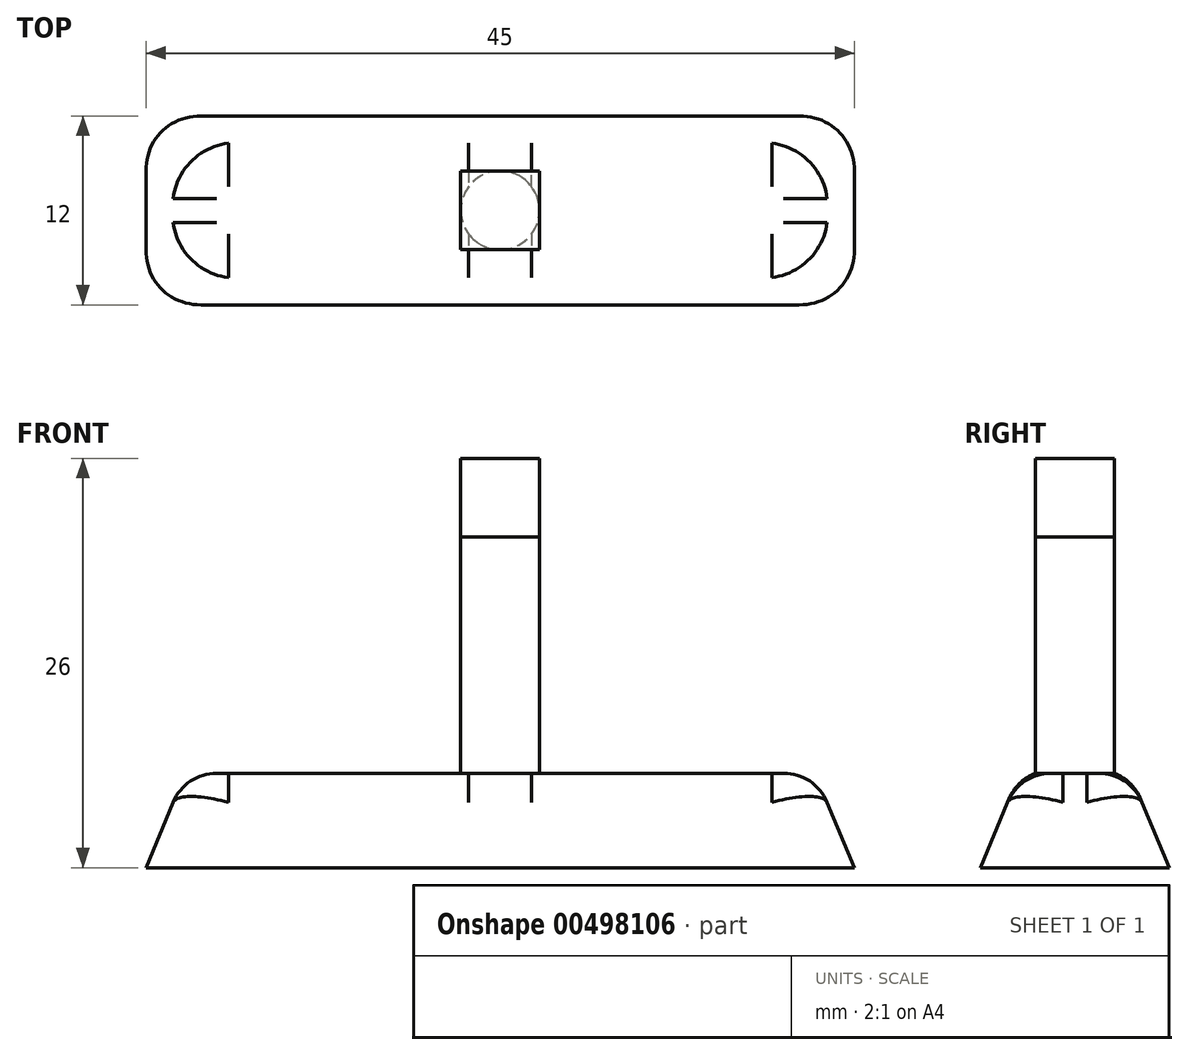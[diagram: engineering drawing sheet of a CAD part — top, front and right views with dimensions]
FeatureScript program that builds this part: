
annotation { "Feature Type Name" : "Feature", "Feature Type Description" : "" }
export const myFeature = defineFeature(function(context is Context, id is Id, definition is map)
    precondition{}
    {
        {
            var Q0;
            Q0=qCreatedBy(makeId("Front.planeOp"),FACE);
            var sketch = newSketch(context, id + "F0", { "sketchPlane" : qUnion([Q0])});
            skLineSegment(sketch, "E0.bottom", {"start": v(22.5, -3) * mm, "end": v(-22.5, -3) * mm});
            skLineSegment(sketch, "E0.top", {"start": v(22.5, 3) * mm, "end": v(-22.5, 3) * mm});
            skLineSegment(sketch, "E0.left", {"start": v(22.5, -3) * mm, "end": v(22.5, 3) * mm});
            skLineSegment(sketch, "E0.right", {"start": v(-22.5, -3) * mm, "end": v(-22.5, 3) * mm});
            skPoint(sketch, "E0.middle", {"position": v(0, 0) * mm});
            skPoint(sketch, "E1", {"position": v(-22.5, 3) * mm});
            skSolve(sketch);
        }
        {
            var Q0;
            Q0 = qSketchRegion(id + "F0", true);
            extrude(context, id + "F1", {"entities" : qUnion([Q0]), "endBound" : BoundingType.SYMMETRIC, "depth" : 12 * mm});
        }
        {
            var Q0;
            Q0=makeQuery(id+"F1.opExtrude","CAP_EDGE",EDGE,{"disambiguationData":[OSD([sQuery(id+"F0.wireOp",EDGE,"E0.top")])],"isStart":false});
            var Q1;
            Q1=makeQuery(id+"F1.opExtrude","SWEPT_EDGE",EDGE,{"disambiguationData":[OSD([sQuery(id+"F0.wireOp",EDGE,"E0.top"),sQuery(id+"F0.wireOp",EDGE,"E0.right")])]});
            var Q2;
            Q2=makeQuery(id+"F1.opExtrude","CAP_EDGE",EDGE,{"disambiguationData":[OSD([sQuery(id+"F0.wireOp",EDGE,"E0.top")])],"isStart":true});
            var Q3;
            Q3=makeQuery(id+"F1.opExtrude","SWEPT_EDGE",EDGE,{"disambiguationData":[OSD([sQuery(id+"F0.wireOp",EDGE,"E0.top"),sQuery(id+"F0.wireOp",EDGE,"E0.left")])]});
            chamfer(context, id + "F2", {"entities" : qUnion([Q0, Q1, Q2, Q3]), "chamferType" : ChamferType.TWO_OFFSETS, "width1" : 6 * mm, "oppositeDirection" : false, "width2" : 2.5 * mm});
        }
        {
            var Q0;
            {var subQ0=sQuery(id+"F0.wireOp",EDGE,"E0.top");Q0=makeQuery(id+"F2.opChamfer","BLEND_EDGE",EDGE,{"blendedFrom":[makeQuery(id+"F1.opExtrude","SWEPT_EDGE",EDGE,{"disambiguationData":[OSD([subQ0,sQuery(id+"F0.wireOp",EDGE,"E0.left")])]}),makeQuery(id+"F1.opExtrude","CAP_EDGE",EDGE,{"disambiguationData":[OSD([subQ0])],"isStart":false})],"blendedInto":[]});}
            var Q1;
            Q1=makeQuery(id+"F1.opExtrude","CAP_EDGE",EDGE,{"disambiguationData":[OSD([sQuery(id+"F0.wireOp",EDGE,"E0.left")])],"isStart":false});
            var Q2;
            Q2=makeQuery(id+"F1.opExtrude","CAP_EDGE",EDGE,{"disambiguationData":[OSD([sQuery(id+"F0.wireOp",EDGE,"E0.left")])],"isStart":true});
            var Q3;
            {var subQ0=sQuery(id+"F0.wireOp",EDGE,"E0.top");Q3=makeQuery(id+"F2.opChamfer","BLEND_EDGE",EDGE,{"blendedFrom":[makeQuery(id+"F1.opExtrude","SWEPT_EDGE",EDGE,{"disambiguationData":[OSD([subQ0,sQuery(id+"F0.wireOp",EDGE,"E0.left")])]}),makeQuery(id+"F1.opExtrude","CAP_EDGE",EDGE,{"disambiguationData":[OSD([subQ0])],"isStart":true})],"blendedInto":[]});}
            var Q4;
            {var subQ0=sQuery(id+"F0.wireOp",EDGE,"E0.top");Q4=makeQuery(id+"F2.opChamfer","BLEND_EDGE",EDGE,{"blendedFrom":[makeQuery(id+"F1.opExtrude","SWEPT_EDGE",EDGE,{"disambiguationData":[OSD([subQ0,sQuery(id+"F0.wireOp",EDGE,"E0.right")])]}),makeQuery(id+"F1.opExtrude","CAP_EDGE",EDGE,{"disambiguationData":[OSD([subQ0])],"isStart":false})],"blendedInto":[]});}
            var Q5;
            Q5=makeQuery(id+"F1.opExtrude","CAP_EDGE",EDGE,{"disambiguationData":[OSD([sQuery(id+"F0.wireOp",EDGE,"E0.right")])],"isStart":false});
            var Q6;
            {var subQ0=sQuery(id+"F0.wireOp",EDGE,"E0.top");Q6=makeQuery(id+"F2.opChamfer","BLEND_EDGE",EDGE,{"blendedFrom":[makeQuery(id+"F1.opExtrude","SWEPT_EDGE",EDGE,{"disambiguationData":[OSD([subQ0,sQuery(id+"F0.wireOp",EDGE,"E0.right")])]}),makeQuery(id+"F1.opExtrude","CAP_EDGE",EDGE,{"disambiguationData":[OSD([subQ0])],"isStart":true})],"blendedInto":[]});}
            var Q7;
            Q7=makeQuery(id+"F1.opExtrude","CAP_EDGE",EDGE,{"disambiguationData":[OSD([sQuery(id+"F0.wireOp",EDGE,"E0.right")])],"isStart":true});
            fillet(context, id + "F3", {"entities" : qUnion([Q0, Q1, Q2, Q3, Q4, Q5, Q6, Q7]), "radius" : 3.8 * mm, "tangentPropagation" : true, "allowEdgeOverflow" : false});
        }
        {
            var Q0;
            Q0=qCreatedBy(makeId("Top.planeOp"),FACE);
            var sketch = newSketch(context, id + "F4", { "sketchPlane" : qUnion([Q0])});
            skCircle(sketch, "E2", {"center": v(0, 0) * mm, "radius": 2.5 * mm});
            skSolve(sketch);
        }
        {
            var Q0;
            Q0 = qSketchRegion(id + "F4", true);
            var Q1;
            Q1=sQuery(id+"F4.wireOp",EDGE,"E2");
            extrude(context, id + "F5", {"entities" : qUnion([Q0]), "operationType" : NewBodyOperationType.ADD, "surfaceEntities" : qUnion([Q1]), "depth" : 18 * mm});
        }
        {
            var Q0;
            {var subQ0=sQuery(id+"F0.wireOp",EDGE,"E0.top");Q0=makeQuery(id+"F2.opChamfer","BLEND_EDGE",EDGE,{"blendedFrom":[makeQuery(id+"F1.opExtrude","CAP_EDGE",EDGE,{"disambiguationData":[OSD([subQ0])],"isStart":false}),makeQuery(id+"F1.opExtrude","SWEPT_FACE",FACE,{"disambiguationData":[OSD([subQ0])]})],"blendedInto":[makeQuery(id+"F1.opExtrude","SWEPT_FACE",FACE,{"disambiguationData":[OSD([subQ0])]})]});}
            var Q1;
            {var subQ0=sQuery(id+"F0.wireOp",EDGE,"E0.top");Q1=makeQuery(id+"F2.opChamfer","BLEND_EDGE",EDGE,{"blendedFrom":[makeQuery(id+"F1.opExtrude","CAP_EDGE",EDGE,{"disambiguationData":[OSD([subQ0])],"isStart":true}),makeQuery(id+"F1.opExtrude","SWEPT_FACE",FACE,{"disambiguationData":[OSD([subQ0])]})],"blendedInto":[makeQuery(id+"F1.opExtrude","SWEPT_FACE",FACE,{"disambiguationData":[OSD([subQ0])]})]});}
            fillet(context, id + "F6", {"entities" : qUnion([Q0, Q1]), "radius" : 3 * mm, "tangentPropagation" : true, "allowEdgeOverflow" : false});
        }
        {
            var Q0;
            Q0=makeQuery(id+"F5.opExtrude","CAP_FACE",FACE,{"disambiguationData":[OSD([sQuery(id+"F4.wireOp",EDGE,"E2")])],"isStart":false});
            var sketch = newSketch(context, id + "F7", { "sketchPlane" : qUnion([Q0])});
            skLineSegment(sketch, "E3.bottom", {"start": v(2.5, 2.5) * mm, "end": v(-2.5, 2.5) * mm});
            skLineSegment(sketch, "E3.top", {"start": v(2.5, -2.5) * mm, "end": v(-2.5, -2.5) * mm});
            skLineSegment(sketch, "E3.left", {"start": v(2.5, 2.5) * mm, "end": v(2.5, -2.5) * mm});
            skLineSegment(sketch, "E3.right", {"start": v(-2.5, 2.5) * mm, "end": v(-2.5, -2.5) * mm});
            skPoint(sketch, "E3.middle", {"position": v(0, 0) * mm});
            skSolve(sketch);
        }
        {
            var Q0;
            {var subQ0=sQuery(id+"F7.wireOp",EDGE,"E3.left");var subQ1=sQuery(id+"F7.wireOp",EDGE,"E3.bottom");var subQ2=makeQuery(id+"F7.imprint","INTERSECT",VERTEX,{"derivedFrom":[subQ1,subQ0]});Q0=makeQuery(id+"F7.imprint","IMPRINT",FACE,{"disambiguationData":[TD([[makeQuery(id+"F7.imprint","IMPRINT",EDGE,{"disambiguationData":[TD([[subQ2,-1.0]])],"derivedFrom":subQ1}),1.0]])]});}
            var Q1;
            {var subQ0=makeQuery(id+"F5.opExtrude","CAP_EDGE",EDGE,{"disambiguationData":[OSD([sQuery(id+"F4.wireOp",EDGE,"E2")])],"isStart":false});var subQ1=makeQuery(id+"F7.imprint","INTERSECT",VERTEX,{"derivedFrom":[subQ0,sQuery(id+"F7.wireOp",EDGE,"E3.bottom")]});Q1=makeQuery(id+"F7.imprint","IMPRINT",FACE,{"disambiguationData":[TD([[makeQuery(id+"F7.imprint","IMPRINT",EDGE,{"disambiguationData":[TD([[subQ1,1.0]])],"derivedFrom":subQ0}),1.0]])]});}
            var Q2;
            {var subQ0=sQuery(id+"F7.wireOp",EDGE,"E3.left");var subQ1=sQuery(id+"F7.wireOp",EDGE,"E3.top");var subQ2=makeQuery(id+"F7.imprint","INTERSECT",VERTEX,{"derivedFrom":[subQ1,subQ0]});Q2=makeQuery(id+"F7.imprint","IMPRINT",FACE,{"disambiguationData":[TD([[makeQuery(id+"F7.imprint","IMPRINT",EDGE,{"disambiguationData":[TD([[subQ2,-1.0]])],"derivedFrom":subQ1}),-1.0]])]});}
            var Q3;
            {var subQ0=sQuery(id+"F7.wireOp",EDGE,"E3.right");var subQ1=sQuery(id+"F7.wireOp",EDGE,"E3.top");var subQ2=makeQuery(id+"F7.imprint","INTERSECT",VERTEX,{"derivedFrom":[subQ1,subQ0]});Q3=makeQuery(id+"F7.imprint","IMPRINT",FACE,{"disambiguationData":[TD([[makeQuery(id+"F7.imprint","IMPRINT",EDGE,{"disambiguationData":[TD([[subQ2,1.0]])],"derivedFrom":subQ1}),-1.0]])]});}
            var Q4;
            {var subQ0=sQuery(id+"F7.wireOp",EDGE,"E3.right");var subQ1=sQuery(id+"F7.wireOp",EDGE,"E3.bottom");var subQ2=makeQuery(id+"F7.imprint","INTERSECT",VERTEX,{"derivedFrom":[subQ1,subQ0]});Q4=makeQuery(id+"F7.imprint","IMPRINT",FACE,{"disambiguationData":[TD([[makeQuery(id+"F7.imprint","IMPRINT",EDGE,{"disambiguationData":[TD([[subQ2,1.0]])],"derivedFrom":subQ1}),1.0]])]});}
            extrude(context, id + "F8", {"entities" : qUnion([Q0, Q1, Q2, Q3, Q4]), "operationType" : NewBodyOperationType.ADD, "depth" : 5 * mm});
        }
    });
